# Revit family: Legrand Armoire XL³ 4000 gaine à câble
name_source: partatom
category: Equipement électrique
units: mm (PartAtom-declared; Revit-internal decimal feet)

## family parameters
Basée sur le plan de construction = Non
Configuration du panneau = Deux colonnes, circuits au sein
Cote de connecteur circulaire = Utiliser le diamètre
Couper avec des vides une fois chargée = Non
Numéro OmniClass = 23.80.30.11.17
Partagée = Non
Point de calcul de pièce = Non
Titre OmniClass = Distribution Boards and Control Panels
Toujours verticalement = Oui
Type d'élément = Tableau de raccordement

## types (6) — shared parameters
Conditions Générale d'Utilisation = https://export.legrand.com
Fabricant = Legrand
Finition = Peinture époxipolyester déposée par poudrage électrostatique
ICW (jusqu'à) = 110
IK avec porte = 08
IK sans porte = 07
IN max (A) = 4000
IP avec porte = 55
IP sans porte = 30
Largeur (mm) = 475 mm  [stored 1.5584 ft]
Matière = Acier
Modèle = XL³ 4000
RAL = 7035
URL = https://www.legrand.fr
zero-valued in all types: Elévation par défaut

## per-type parameters (varying)
| type | Hauteur (mm) | profondeur (mm) |
| 020501-020500-020511-020554 | 2000 mm  [stored 6.56168 ft] | 475 mm  [stored 1.5584 ft] |
| 020501-020850-020511-020861 | 2200 mm | 475 mm  [stored 1.5584 ft] |
| 020502-020500-020514-020554 | 2000 mm  [stored 6.56168 ft] | 725 mm  [stored 2.37861 ft] |
| 020502-020850-020514-020861 | 2200 mm | 725 mm  [stored 2.37861 ft] |
| 020503-020500-020517-020554 | 2000 mm  [stored 6.56168 ft] | 975 mm  [stored 3.19882 ft] |
| 020503-020850-020517-020861 | 2200 mm | 975 mm  [stored 3.19882 ft] |

note: [stored X ft] marks values corroborated as IEEE doubles in the binary element streams (Revit-internal decimal feet)
